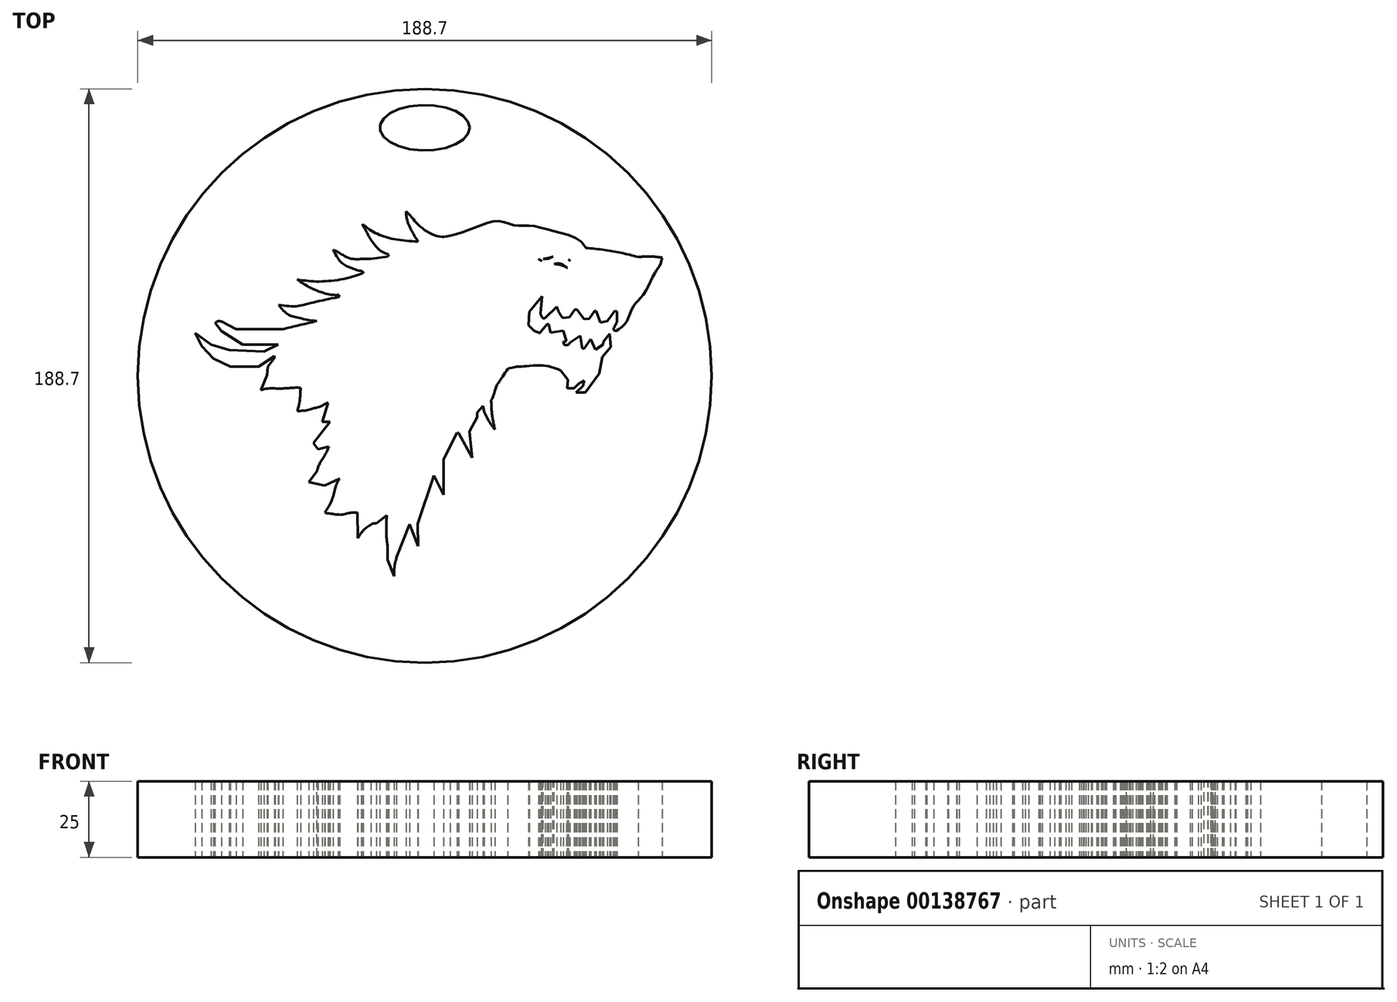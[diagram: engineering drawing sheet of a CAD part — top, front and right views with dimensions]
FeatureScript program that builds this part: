
annotation { "Feature Type Name" : "Feature", "Feature Type Description" : "" }
export const myFeature = defineFeature(function(context is Context, id is Id, definition is map)
    precondition{}
    {
        {
            var Q0;
            Q0=qCreatedBy(makeId("Top.planeOp"),FACE);
            var sketch = newSketch(context, id + "F0", { "sketchPlane" : qUnion([Q0])});
            skLineSegment(sketch, "E0", {"start": v(0, -46.34) * mm, "end": v(0, 97.64) * mm, "construction": true});
            skLineSegment(sketch, "E1", {"start": v(-98.9, 0) * mm, "end": v(160.67, 0) * mm, "construction": true});
            skFitSpline(sketch, "E2", {"points": [v(8.37, 46.02) * mm, v(16.5, 48.73) * mm, v(24.2, 50.9) * mm, v(29.67, 49.45) * mm, v(34.86, 49.36) * mm, v(43.4, 47.27) * mm, v(53, 42.06) * mm], "startDerivative": vector(47.53, 12.6) * mm, "endDerivative": vector(25.31, -53.78) * mm});
            skFitSpline(sketch, "E3", {"points": [v(53, 42.06) * mm, v(61.93, 40.92) * mm, v(70.2, 39.06) * mm], "startDerivative": vector(17.28, -1.4) * mm, "endDerivative": vector(17.12, -4.59) * mm});
            skFitSpline(sketch, "E4", {"points": [v(70.2, 39.06) * mm, v(73.91, 39.25) * mm, v(78, 38.88) * mm], "startDerivative": vector(7.53, 0.65) * mm, "endDerivative": vector(8.07, -1) * mm});
            skFitSpline(sketch, "E5", {"points": [v(78, 38.88) * mm, v(77.15, 36.05) * mm, v(75.57, 33.69) * mm, v(71.82, 26.58) * mm, v(68.71, 23.01) * mm, v(66.37, 17.92) * mm, v(62.79, 14.7) * mm], "startDerivative": vector(-2.44, -23.85) * mm, "endDerivative": vector(-25.04, -14.1) * mm});
            skLineSegment(sketch, "E6", {"start": v(62.79, 14.7) * mm, "end": v(62, 15.24) * mm});
            skLineSegment(sketch, "E7", {"start": v(62, 15.24) * mm, "end": v(63.2, 17.7) * mm});
            skLineSegment(sketch, "E8", {"start": v(63.2, 17.7) * mm, "end": v(63.2, 21.18) * mm});
            skLineSegment(sketch, "E9", {"start": v(63.2, 21.18) * mm, "end": v(62.45, 21.32) * mm});
            skLineSegment(sketch, "E10", {"start": v(62.45, 21.32) * mm, "end": v(60.09, 17.98) * mm});
            skLineSegment(sketch, "E11", {"start": v(60.09, 17.98) * mm, "end": v(57.72, 17.51) * mm});
            skLineSegment(sketch, "E12", {"start": v(57.72, 17.51) * mm, "end": v(56.32, 21.32) * mm});
            skLineSegment(sketch, "E13", {"start": v(56.32, 21.32) * mm, "end": v(55.78, 21.31) * mm});
            skLineSegment(sketch, "E14", {"start": v(55.78, 21.31) * mm, "end": v(54.02, 18.83) * mm});
            skLineSegment(sketch, "E15", {"start": v(54.02, 18.83) * mm, "end": v(52.38, 18.64) * mm});
            skLineSegment(sketch, "E16", {"start": v(52.38, 18.64) * mm, "end": v(49.96, 21.76) * mm});
            skLineSegment(sketch, "E17", {"start": v(49.96, 21.76) * mm, "end": v(49.36, 21.76) * mm});
            skLineSegment(sketch, "E18", {"start": v(49.36, 21.76) * mm, "end": v(47.55, 19.25) * mm});
            skLineSegment(sketch, "E19", {"start": v(47.55, 19.25) * mm, "end": v(45.5, 19.02) * mm});
            skFitSpline(sketch, "E20", {"points": [v(45.5, 19.02) * mm, v(44.43, 20.33) * mm, v(43.4, 22.76) * mm], "startDerivative": vector(-3.09, 1.68) * mm, "endDerivative": vector(-1.4, 5.58) * mm});
            skLineSegment(sketch, "E21", {"start": v(43.4, 22.76) * mm, "end": v(39.6, 19.05) * mm});
            skLineSegment(sketch, "E22", {"start": v(38.55, 26.15) * mm, "end": v(38.05, 20.53) * mm});
            skFitSpline(sketch, "E23", {"points": [v(38.05, 20.53) * mm, v(38.32, 19.7) * mm, v(38.9, 18.95) * mm, v(39.6, 19.05) * mm], "startDerivative": vector(0.59, -2.33) * mm, "endDerivative": vector(2.36, 0.9) * mm});
            skLineSegment(sketch, "E24", {"start": v(38.55, 26.15) * mm, "end": v(34.4, 21.11) * mm});
            skLineSegment(sketch, "E25", {"start": v(34.4, 21.11) * mm, "end": v(34.15, 16.58) * mm});
            skFitSpline(sketch, "E26", {"points": [v(34.15, 16.58) * mm, v(35.74, 14.98) * mm, v(37.83, 14.05) * mm], "startDerivative": vector(3.39, -3.5) * mm, "endDerivative": vector(3.98, -1.53) * mm});
            skLineSegment(sketch, "E27", {"start": v(37.83, 14.05) * mm, "end": v(40.2, 16.98) * mm});
            skLineSegment(sketch, "E28", {"start": v(40.2, 16.98) * mm, "end": v(40.7, 16.98) * mm});
            skLineSegment(sketch, "E29", {"start": v(40.7, 16.98) * mm, "end": v(41.3, 14.23) * mm});
            skLineSegment(sketch, "E30", {"start": v(41.3, 14.23) * mm, "end": v(45.53, 14.8) * mm});
            skLineSegment(sketch, "E31", {"start": v(45.53, 14.8) * mm, "end": v(46.61, 11.43) * mm});
            skLineSegment(sketch, "E32", {"start": v(46.61, 11.43) * mm, "end": v(45.6, 11.1) * mm});
            skLineSegment(sketch, "E33", {"start": v(47.71, 10.9) * mm, "end": v(51.18, 13.14) * mm});
            skFitSpline(sketch, "E34", {"points": [v(47.71, 10.9) * mm, v(47.14, 10.2) * mm, v(45.87, 10.24) * mm, v(45.6, 11.1) * mm], "startDerivative": vector(-1.25, -2.64) * mm, "endDerivative": vector(-0.16, 3.24) * mm});
            skLineSegment(sketch, "E35", {"start": v(51.18, 13.14) * mm, "end": v(51.76, 8.96) * mm});
            skLineSegment(sketch, "E36", {"start": v(51.76, 8.96) * mm, "end": v(52.35, 8.96) * mm});
            skLineSegment(sketch, "E37", {"start": v(52.35, 8.96) * mm, "end": v(54.64, 12.02) * mm});
            skLineSegment(sketch, "E38", {"start": v(54.64, 12.02) * mm, "end": v(56.15, 8.66) * mm});
            skLineSegment(sketch, "E39", {"start": v(56.15, 8.66) * mm, "end": v(58.7, 10.29) * mm});
            skLineSegment(sketch, "E40", {"start": v(58.7, 10.29) * mm, "end": v(58.8, 11.25) * mm});
            skLineSegment(sketch, "E41", {"start": v(58.8, 11.25) * mm, "end": v(60.75, 13.83) * mm});
            skLineSegment(sketch, "E42", {"start": v(60.75, 13.83) * mm, "end": v(61.12, 9.51) * mm});
            skLineSegment(sketch, "E43", {"start": v(61.12, 9.51) * mm, "end": v(58.37, 6.23) * mm});
            skLineSegment(sketch, "E44", {"start": v(58.37, 6.23) * mm, "end": v(57.38, 0.75) * mm});
            skLineSegment(sketch, "E45", {"start": v(57.38, 0.75) * mm, "end": v(52.78, -5.5) * mm});
            skLineSegment(sketch, "E46", {"start": v(52.78, -5.5) * mm, "end": v(49.73, -5.5) * mm});
            skLineSegment(sketch, "E47", {"start": v(49.73, -5.5) * mm, "end": v(52, -3.3) * mm});
            skLineSegment(sketch, "E48", {"start": v(52, -3.3) * mm, "end": v(52.42, -1.58) * mm});
            skLineSegment(sketch, "E49", {"start": v(52.42, -1.58) * mm, "end": v(50.65, -2.56) * mm});
            skLineSegment(sketch, "E50", {"start": v(50.65, -2.56) * mm, "end": v(49.07, -4.09) * mm});
            skLineSegment(sketch, "E51", {"start": v(49.07, -4.09) * mm, "end": v(46.86, -4.09) * mm});
            skLineSegment(sketch, "E52", {"start": v(46.86, -4.09) * mm, "end": v(47.02, -1.26) * mm});
            skLineSegment(sketch, "E53", {"start": v(47.02, -1.26) * mm, "end": v(44.6, 1.8) * mm});
            skFitSpline(sketch, "E54", {"points": [v(44.6, 1.8) * mm, v(38.62, 3.43) * mm, v(31.22, 2.96) * mm, v(30.22, 2.96) * mm, v(27.26, 2.3) * mm], "startDerivative": vector(-17, 7.19) * mm, "endDerivative": vector(-16.02, -4.1) * mm});
            skFitSpline(sketch, "E55", {"points": [v(27.26, 2.3) * mm, v(24.24, -2.27) * mm, v(23.71, -3.01) * mm, v(23.18, -4.49) * mm, v(21.86, -8.07) * mm], "startDerivative": vector(-9.48, -15.13) * mm, "endDerivative": vector(-7.44, -13.5) * mm});
            skFitSpline(sketch, "E56", {"points": [v(21.86, -8.07) * mm, v(22.1, -12.6) * mm, v(23.06, -17.73) * mm], "startDerivative": vector(0.3, -9.94) * mm, "endDerivative": vector(2.15, -9.73) * mm});
            skLineSegment(sketch, "E57", {"start": v(19.14, -9.9) * mm, "end": v(19.48, -11.87) * mm});
            skFitSpline(sketch, "E58", {"points": [v(19.48, -11.87) * mm, v(20.92, -14.56) * mm, v(23.06, -17.73) * mm], "startDerivative": vector(3.02, -5.51) * mm, "endDerivative": vector(4.86, -6.04) * mm});
            skLineSegment(sketch, "E59", {"start": v(19.14, -9.9) * mm, "end": v(17.18, -12.06) * mm});
            skLineSegment(sketch, "E60", {"start": v(17.18, -12.06) * mm, "end": v(17.18, -13.56) * mm});
            skLineSegment(sketch, "E61", {"start": v(17.18, -13.56) * mm, "end": v(14.64, -18.29) * mm});
            skLineSegment(sketch, "E62", {"start": v(14.64, -18.29) * mm, "end": v(15.58, -26.93) * mm});
            skLineSegment(sketch, "E63", {"start": v(15.58, -26.93) * mm, "end": v(11.12, -18.85) * mm});
            skLineSegment(sketch, "E64", {"start": v(11.12, -18.85) * mm, "end": v(10.6, -18.76) * mm});
            skLineSegment(sketch, "E65", {"start": v(10.6, -18.76) * mm, "end": v(6.22, -27.44) * mm});
            skLineSegment(sketch, "E66", {"start": v(6.22, -27.44) * mm, "end": v(6.17, -39.18) * mm});
            skLineSegment(sketch, "E67", {"start": v(6.17, -39.18) * mm, "end": v(3.07, -32.74) * mm});
            skLineSegment(sketch, "E68", {"start": v(3.07, -32.74) * mm, "end": v(-2.3, -48.66) * mm});
            skLineSegment(sketch, "E69", {"start": v(-2.3, -48.66) * mm, "end": v(-2.17, -56.06) * mm});
            skLineSegment(sketch, "E70", {"start": v(-2.17, -56.06) * mm, "end": v(-4.99, -48.79) * mm});
            skLineSegment(sketch, "E71", {"start": v(-4.99, -48.79) * mm, "end": v(-9.28, -59.71) * mm});
            skFitSpline(sketch, "E72", {"points": [v(-9.28, -59.71) * mm, v(-9.83, -61.89) * mm, v(-10.04, -63.68) * mm, v(-10.08, -65.99) * mm], "startDerivative": vector(-1.5, -7.23) * mm, "endDerivative": vector(0.61, -9.45) * mm});
            skLineSegment(sketch, "E73", {"start": v(-10.08, -65.99) * mm, "end": v(-12.22, -60.51) * mm});
            skLineSegment(sketch, "E74", {"start": v(-12.22, -60.51) * mm, "end": v(-12.22, -55.67) * mm});
            skFitSpline(sketch, "E75", {"points": [v(-12.22, -55.67) * mm, v(-12.62, -52.29) * mm, v(-12.62, -47.83) * mm, v(-12.44, -45.9) * mm], "startDerivative": vector(-2.35, 9.95) * mm, "endDerivative": vector(0.6, 6.7) * mm});
            skLineSegment(sketch, "E76", {"start": v(-12.44, -45.9) * mm, "end": v(-15.86, -48.6) * mm});
            skFitSpline(sketch, "E77", {"points": [v(-15.86, -48.6) * mm, v(-16.85, -48.6) * mm, v(-19.68, -50.34) * mm, v(-21.96, -53.33) * mm], "startDerivative": vector(-4.67, 0.75) * mm, "endDerivative": vector(-4.96, -8.28) * mm});
            skLineSegment(sketch, "E78", {"start": v(-21.96, -53.33) * mm, "end": v(-22.2, -45.03) * mm});
            skFitSpline(sketch, "E79", {"points": [v(-22.2, -45.03) * mm, v(-23.7, -45.03) * mm, v(-25.38, -45.24) * mm, v(-27.7, -45.69) * mm, v(-30.45, -45.39) * mm, v(-32.84, -45.03) * mm], "startDerivative": vector(-10.12, -0.25) * mm, "endDerivative": vector(-8.12, 2.64) * mm});
            skFitSpline(sketch, "E80", {"points": [v(-32.84, -45.03) * mm, v(-30.46, -40.57) * mm, v(-29.33, -36.68) * mm, v(-27.93, -33.79) * mm], "startDerivative": vector(7.96, 12) * mm, "endDerivative": vector(7.34, 9.15) * mm});
            skLineSegment(sketch, "E81", {"start": v(-27.93, -33.79) * mm, "end": v(-33, -36.1) * mm});
            skLineSegment(sketch, "E82", {"start": v(-33, -36.1) * mm, "end": v(-38.14, -34.9) * mm});
            skLineSegment(sketch, "E83", {"start": v(-38.14, -34.9) * mm, "end": v(-35.38, -31.25) * mm});
            skFitSpline(sketch, "E84", {"points": [v(-35.38, -31.25) * mm, v(-34.63, -29.02) * mm, v(-32.62, -25.74) * mm, v(-31.58, -23.28) * mm], "startDerivative": vector(1.7, 7.16) * mm, "endDerivative": vector(2.6, 7.43) * mm});
            skLineSegment(sketch, "E85", {"start": v(-31.58, -23.28) * mm, "end": v(-35.08, -24.1) * mm});
            skLineSegment(sketch, "E86", {"start": v(-35.08, -24.1) * mm, "end": v(-36.57, -22.16) * mm});
            skLineSegment(sketch, "E87", {"start": v(-36.57, -22.16) * mm, "end": v(-31.2, -15.15) * mm});
            skLineSegment(sketch, "E88", {"start": v(-31.2, -15.15) * mm, "end": v(-33.74, -15.15) * mm});
            skLineSegment(sketch, "E89", {"start": v(-33.74, -15.15) * mm, "end": v(-31.79, -8.9) * mm});
            skFitSpline(sketch, "E90", {"points": [v(-31.79, -8.9) * mm, v(-33.97, -9.91) * mm, v(-36.14, -10.62) * mm, v(-38.4, -11.28) * mm, v(-41.9, -11.6) * mm], "startDerivative": vector(-6.1, 1.36) * mm, "endDerivative": vector(-8.76, -0.8) * mm});
            skFitSpline(sketch, "E91", {"points": [v(-41.9, -11.6) * mm, v(-41.13, -8.29) * mm, v(-40.83, -3.95) * mm], "startDerivative": vector(1.85, 6.75) * mm, "endDerivative": vector(0.43, 8.1) * mm});
            skFitSpline(sketch, "E92", {"points": [v(-40.83, -3.95) * mm, v(-45.11, -4.06) * mm, v(-48.54, -4.17) * mm, v(-53.9, -4.78) * mm], "startDerivative": vector(-10.76, 1.27) * mm, "endDerivative": vector(-11.93, -6.43) * mm});
            skLineSegment(sketch, "E93", {"start": v(-53.9, -4.78) * mm, "end": v(-51.88, 0.27) * mm});
            skLineSegment(sketch, "E94", {"start": v(-51.88, 0.27) * mm, "end": v(-51.63, 3.08) * mm});
            skLineSegment(sketch, "E95", {"start": v(-51.63, 3.08) * mm, "end": v(-49.22, 6.21) * mm});
            skLineSegment(sketch, "E96", {"start": v(-49.22, 6.21) * mm, "end": v(-49.5, 6.43) * mm});
            skLineSegment(sketch, "E97", {"start": v(-49.5, 6.43) * mm, "end": v(-54.64, 2.98) * mm});
            skLineSegment(sketch, "E98", {"start": v(-54.64, 2.98) * mm, "end": v(-63.96, 2.98) * mm});
            skLineSegment(sketch, "E99", {"start": v(-63.96, 2.98) * mm, "end": v(-69.48, 5.65) * mm});
            skLineSegment(sketch, "E100", {"start": v(-69.48, 5.65) * mm, "end": v(-73.26, 9.73) * mm});
            skLineSegment(sketch, "E101", {"start": v(-73.26, 9.73) * mm, "end": v(-75.45, 14.1) * mm});
            skLineSegment(sketch, "E102", {"start": v(-75.45, 14.1) * mm, "end": v(-70.28, 10.27) * mm});
            skLineSegment(sketch, "E103", {"start": v(-70.28, 10.27) * mm, "end": v(-64.26, 8.53) * mm});
            skLineSegment(sketch, "E104", {"start": v(-64.26, 8.53) * mm, "end": v(-52.92, 7.99) * mm});
            skLineSegment(sketch, "E105", {"start": v(-52.92, 7.99) * mm, "end": v(-48.15, 10.22) * mm});
            skLineSegment(sketch, "E106", {"start": v(-48.15, 10.22) * mm, "end": v(-59.86, 10.22) * mm});
            skLineSegment(sketch, "E107", {"start": v(-59.86, 10.22) * mm, "end": v(-66.87, 14.75) * mm});
            skLineSegment(sketch, "E108", {"start": v(-66.87, 14.75) * mm, "end": v(-68.94, 17.44) * mm});
            skLineSegment(sketch, "E109", {"start": v(-66.8, 17.83) * mm, "end": v(-62.02, 15.35) * mm});
            skLineSegment(sketch, "E110", {"start": v(-62.02, 15.35) * mm, "end": v(-46.65, 15.35) * mm});
            skFitSpline(sketch, "E111", {"points": [v(-46.65, 15.35) * mm, v(-41.43, 16.6) * mm, v(-35.5, 17.98) * mm], "startDerivative": vector(10.61, 2.53) * mm, "endDerivative": vector(11.66, 2.74) * mm});
            skFitSpline(sketch, "E112", {"points": [v(-35.5, 17.98) * mm, v(-41.82, 19.11) * mm, v(-44.94, 20.17) * mm, v(-48, 23.3) * mm], "startDerivative": vector(-16.98, 1.76) * mm, "endDerivative": vector(-6.9, 10.96) * mm});
            skFitSpline(sketch, "E113", {"points": [v(-48, 23.3) * mm, v(-42.22, 22.9) * mm, v(-37.6, 23.9) * mm, v(-28.48, 25.89) * mm], "startDerivative": vector(19.28, -2.54) * mm, "endDerivative": vector(24.98, 5.08) * mm});
            skFitSpline(sketch, "E114", {"points": [v(-28.48, 26.58) * mm, v(-31.56, 26.78) * mm, v(-37.4, 28.87) * mm, v(-41.92, 31.66) * mm], "startDerivative": vector(-10.5, -0.18) * mm, "endDerivative": vector(-11.9, 8.2) * mm});
            skArc(sketch, "E115", {"start": v(-28.48, 25.89) * mm, "mid": v(-28.12, 26.23) * mm, "end": v(-28.48, 26.58) * mm});
            skFitSpline(sketch, "E116", {"points": [v(-68.94, 17.44) * mm, v(-67.92, 17.97) * mm, v(-66.8, 17.83) * mm], "startDerivative": vector(1.97, 1.4) * mm, "endDerivative": vector(2.31, -0.6) * mm});
            skFitSpline(sketch, "E117", {"points": [v(-41.92, 31.66) * mm, v(-36.84, 31.05) * mm, v(-31.36, 31.2) * mm, v(-24.7, 32.3) * mm, v(-20.72, 33.69) * mm], "startDerivative": vector(20.83, -3.13) * mm, "endDerivative": vector(16.42, 6.68) * mm});
            skFitSpline(sketch, "E118", {"points": [v(-20.72, 33.69) * mm, v(-20.23, 34.03) * mm, v(-20.92, 34.48) * mm], "startDerivative": vector(2.1, 0.45) * mm, "endDerivative": vector(-2.36, 1.12) * mm});
            skFitSpline(sketch, "E119", {"points": [v(-20.92, 34.48) * mm, v(-24.7, 35.66) * mm, v(-27.36, 37.18) * mm, v(-30.15, 41.53) * mm], "startDerivative": vector(-10.4, 0.84) * mm, "endDerivative": vector(-5.33, 11.62) * mm});
            skFitSpline(sketch, "E120", {"points": [v(-30.15, 41.53) * mm, v(-27.9, 40.27) * mm, v(-24.38, 38.58) * mm, v(-20.96, 38.41) * mm, v(-17.67, 38.48) * mm], "startDerivative": vector(9.55, -5.2) * mm, "endDerivative": vector(13.09, 0.11) * mm});
            skLineSegment(sketch, "E121", {"start": v(-17.67, 38.48) * mm, "end": v(-12.16, 39.28) * mm});
            skLineSegment(sketch, "E122", {"start": v(-12.16, 39.28) * mm, "end": v(-11.8, 39.9) * mm});
            skFitSpline(sketch, "E123", {"points": [v(-11.8, 39.9) * mm, v(-14.65, 41.23) * mm, v(-17.8, 44.9) * mm, v(-18.97, 46.96) * mm, v(-20.52, 49.83) * mm], "startDerivative": vector(-11.73, 3.62) * mm, "endDerivative": vector(-6.78, 12.4) * mm});
            skFitSpline(sketch, "E124", {"points": [v(-20.52, 49.83) * mm, v(-16.53, 47.15) * mm, v(-10.66, 45.04) * mm, v(-2.16, 44.15) * mm], "startDerivative": vector(13.1, -9.77) * mm, "endDerivative": vector(23.04, -1.36) * mm});
            skFitSpline(sketch, "E125", {"points": [v(-2.16, 44.15) * mm, v(-3.8, 46.7) * mm, v(-5.85, 51.28) * mm, v(-6.14, 54.04) * mm], "startDerivative": vector(-5.04, 7.36) * mm, "endDerivative": vector(-0.06, 8.63) * mm});
            skFitSpline(sketch, "E126", {"points": [v(-6.14, 54.04) * mm, v(-4.54, 52.44) * mm, v(-1.41, 49.01) * mm, v(4.44, 45.88) * mm, v(8.37, 46.02) * mm], "startDerivative": vector(8.45, -7.78) * mm, "endDerivative": vector(15.33, 2.76) * mm});
            skFitSpline(sketch, "E127", {"points": [v(37.42, 38.31) * mm, v(40.78, 37) * mm, v(44.4, 36.52) * mm, v(47.82, 34.96) * mm], "startDerivative": vector(9.91, -4.83) * mm, "endDerivative": vector(9.8, -5.8) * mm});
            skFitSpline(sketch, "E128", {"points": [v(37.42, 38.31) * mm, v(40.89, 38.8) * mm, v(43.76, 39.66) * mm, v(46.07, 39.28) * mm, v(47.7, 37.83) * mm], "startDerivative": vector(15.86, 1.57) * mm, "endDerivative": vector(4.95, -5.03) * mm});
            skLineSegment(sketch, "E129", {"start": v(47.7, 37.83) * mm, "end": v(47.82, 34.96) * mm});
            skSolve(sketch);
        }
        {
            var Q0;
            Q0=makeQuery(id+"F0.imprint","IMPRINT",FACE,{"disambiguationData":[TD([[makeQuery(id+"F0.imprint","IMPRINT",EDGE,{"derivedFrom":sQuery(id+"F0.wireOp",EDGE,"E2")}),-1.0]])]});
            extrude(context, id + "F1", {"entities" : qUnion([Q0]), "depth" : 25 * mm});
        }
        {
            var Q0;
            Q0=qCreatedBy(makeId("Top.planeOp"),FACE);
            var sketch = newSketch(context, id + "F2", { "sketchPlane" : qUnion([Q0])});
            skCircle(sketch, "E130", {"center": v(0, 0) * mm, "radius": 94.35 * mm});
            skEllipse(sketch, "E131", {"center": v(0, 81.58) * mm, "majorRadius": 14.76 * mm, "minorRadius": 7.47 * mm, "majorAxis": v(1, 0)});
            skSolve(sketch);
        }
        {
            var Q0;
            Q0=makeQuery(id+"F2.imprint","IMPRINT",FACE,{"disambiguationData":[TD([[makeQuery(id+"F2.imprint","IMPRINT",EDGE,{"derivedFrom":sQuery(id+"F2.wireOp",EDGE,"E130")}),1.0]])]});
            extrude(context, id + "F3", {"entities" : qUnion([Q0]), "depth" : 25 * mm});
        }
        {
            var Q0;
            Q0=makeQuery(id+"F1.opExtrude","SWEPT_BODY",BODY,{"disambiguationData":[OSD([sQuery(id+"F0.wireOp",EDGE,"E2"),sQuery(id+"F0.wireOp",EDGE,"E3"),sQuery(id+"F0.wireOp",EDGE,"E4"),sQuery(id+"F0.wireOp",EDGE,"E5"),sQuery(id+"F0.wireOp",EDGE,"E6"),sQuery(id+"F0.wireOp",EDGE,"E7"),sQuery(id+"F0.wireOp",EDGE,"E8"),sQuery(id+"F0.wireOp",EDGE,"E9"),sQuery(id+"F0.wireOp",EDGE,"E10"),sQuery(id+"F0.wireOp",EDGE,"E11"),sQuery(id+"F0.wireOp",EDGE,"E12"),sQuery(id+"F0.wireOp",EDGE,"E13"),sQuery(id+"F0.wireOp",EDGE,"E14"),sQuery(id+"F0.wireOp",EDGE,"E15"),sQuery(id+"F0.wireOp",EDGE,"E16"),sQuery(id+"F0.wireOp",EDGE,"E17"),sQuery(id+"F0.wireOp",EDGE,"E18"),sQuery(id+"F0.wireOp",EDGE,"E19"),sQuery(id+"F0.wireOp",EDGE,"E20"),sQuery(id+"F0.wireOp",EDGE,"E21"),sQuery(id+"F0.wireOp",EDGE,"E22"),sQuery(id+"F0.wireOp",EDGE,"E23"),sQuery(id+"F0.wireOp",EDGE,"E24"),sQuery(id+"F0.wireOp",EDGE,"E25"),sQuery(id+"F0.wireOp",EDGE,"E26"),sQuery(id+"F0.wireOp",EDGE,"E27"),sQuery(id+"F0.wireOp",EDGE,"E28"),sQuery(id+"F0.wireOp",EDGE,"E29"),sQuery(id+"F0.wireOp",EDGE,"E30"),sQuery(id+"F0.wireOp",EDGE,"E31"),sQuery(id+"F0.wireOp",EDGE,"E32"),sQuery(id+"F0.wireOp",EDGE,"E33"),sQuery(id+"F0.wireOp",EDGE,"E34"),sQuery(id+"F0.wireOp",EDGE,"E35"),sQuery(id+"F0.wireOp",EDGE,"E36"),sQuery(id+"F0.wireOp",EDGE,"E37"),sQuery(id+"F0.wireOp",EDGE,"E38"),sQuery(id+"F0.wireOp",EDGE,"E39"),sQuery(id+"F0.wireOp",EDGE,"E40"),sQuery(id+"F0.wireOp",EDGE,"E41"),sQuery(id+"F0.wireOp",EDGE,"E42"),sQuery(id+"F0.wireOp",EDGE,"E43"),sQuery(id+"F0.wireOp",EDGE,"E44"),sQuery(id+"F0.wireOp",EDGE,"E45"),sQuery(id+"F0.wireOp",EDGE,"E46"),sQuery(id+"F0.wireOp",EDGE,"E47"),sQuery(id+"F0.wireOp",EDGE,"E48"),sQuery(id+"F0.wireOp",EDGE,"E49"),sQuery(id+"F0.wireOp",EDGE,"E50"),sQuery(id+"F0.wireOp",EDGE,"E51"),sQuery(id+"F0.wireOp",EDGE,"E52"),sQuery(id+"F0.wireOp",EDGE,"E53"),sQuery(id+"F0.wireOp",EDGE,"E54"),sQuery(id+"F0.wireOp",EDGE,"E55"),sQuery(id+"F0.wireOp",EDGE,"E56"),sQuery(id+"F0.wireOp",EDGE,"E57"),sQuery(id+"F0.wireOp",EDGE,"E58"),sQuery(id+"F0.wireOp",EDGE,"E59"),sQuery(id+"F0.wireOp",EDGE,"E60"),sQuery(id+"F0.wireOp",EDGE,"E61"),sQuery(id+"F0.wireOp",EDGE,"E62"),sQuery(id+"F0.wireOp",EDGE,"E63"),sQuery(id+"F0.wireOp",EDGE,"E64"),sQuery(id+"F0.wireOp",EDGE,"E65"),sQuery(id+"F0.wireOp",EDGE,"E66"),sQuery(id+"F0.wireOp",EDGE,"E67"),sQuery(id+"F0.wireOp",EDGE,"E68"),sQuery(id+"F0.wireOp",EDGE,"E69"),sQuery(id+"F0.wireOp",EDGE,"E70"),sQuery(id+"F0.wireOp",EDGE,"E71"),sQuery(id+"F0.wireOp",EDGE,"E72"),sQuery(id+"F0.wireOp",EDGE,"E73"),sQuery(id+"F0.wireOp",EDGE,"E74"),sQuery(id+"F0.wireOp",EDGE,"E75"),sQuery(id+"F0.wireOp",EDGE,"E76"),sQuery(id+"F0.wireOp",EDGE,"E77"),sQuery(id+"F0.wireOp",EDGE,"E78"),sQuery(id+"F0.wireOp",EDGE,"E79"),sQuery(id+"F0.wireOp",EDGE,"E80"),sQuery(id+"F0.wireOp",EDGE,"E81"),sQuery(id+"F0.wireOp",EDGE,"E82"),sQuery(id+"F0.wireOp",EDGE,"E83"),sQuery(id+"F0.wireOp",EDGE,"E84"),sQuery(id+"F0.wireOp",EDGE,"E85"),sQuery(id+"F0.wireOp",EDGE,"E86"),sQuery(id+"F0.wireOp",EDGE,"E87"),sQuery(id+"F0.wireOp",EDGE,"E88"),sQuery(id+"F0.wireOp",EDGE,"E89"),sQuery(id+"F0.wireOp",EDGE,"E90"),sQuery(id+"F0.wireOp",EDGE,"E91"),sQuery(id+"F0.wireOp",EDGE,"E92"),sQuery(id+"F0.wireOp",EDGE,"E93"),sQuery(id+"F0.wireOp",EDGE,"E94"),sQuery(id+"F0.wireOp",EDGE,"E95"),sQuery(id+"F0.wireOp",EDGE,"E96"),sQuery(id+"F0.wireOp",EDGE,"E97"),sQuery(id+"F0.wireOp",EDGE,"E98"),sQuery(id+"F0.wireOp",EDGE,"E99"),sQuery(id+"F0.wireOp",EDGE,"E100"),sQuery(id+"F0.wireOp",EDGE,"E101"),sQuery(id+"F0.wireOp",EDGE,"E102"),sQuery(id+"F0.wireOp",EDGE,"E103"),sQuery(id+"F0.wireOp",EDGE,"E104"),sQuery(id+"F0.wireOp",EDGE,"E105"),sQuery(id+"F0.wireOp",EDGE,"E106"),sQuery(id+"F0.wireOp",EDGE,"E107"),sQuery(id+"F0.wireOp",EDGE,"E108"),sQuery(id+"F0.wireOp",EDGE,"E109"),sQuery(id+"F0.wireOp",EDGE,"E110"),sQuery(id+"F0.wireOp",EDGE,"E111"),sQuery(id+"F0.wireOp",EDGE,"E112"),sQuery(id+"F0.wireOp",EDGE,"E113"),sQuery(id+"F0.wireOp",EDGE,"E114"),sQuery(id+"F0.wireOp",EDGE,"E115"),sQuery(id+"F0.wireOp",EDGE,"E116"),sQuery(id+"F0.wireOp",EDGE,"E117"),sQuery(id+"F0.wireOp",EDGE,"E118"),sQuery(id+"F0.wireOp",EDGE,"E119"),sQuery(id+"F0.wireOp",EDGE,"E120"),sQuery(id+"F0.wireOp",EDGE,"E121"),sQuery(id+"F0.wireOp",EDGE,"E122"),sQuery(id+"F0.wireOp",EDGE,"E123"),sQuery(id+"F0.wireOp",EDGE,"E124"),sQuery(id+"F0.wireOp",EDGE,"E125"),sQuery(id+"F0.wireOp",EDGE,"E126"),sQuery(id+"F0.wireOp",EDGE,"E127"),sQuery(id+"F0.wireOp",EDGE,"E128"),sQuery(id+"F0.wireOp",EDGE,"E129")])]});
            var Q1;
            Q1=makeQuery(id+"F3.opExtrude","SWEPT_BODY",BODY,{"disambiguationData":[OSD([sQuery(id+"F2.wireOp",EDGE,"E130"),sQuery(id+"F2.wireOp",EDGE,"E131")])]});
            booleanBodies(context, id + "F4", {"operationType" : BooleanOperationType.SUBTRACTION, "tools" : qUnion([Q0]), "targets" : qUnion([Q1])});
        }
        {
            var Q0;
            {var subQ0=sQuery(id+"F2.wireOp",EDGE,"E130");var subQ1=sQuery(id+"F2.wireOp",EDGE,"E131");Q0=makeQuery(id+"F4.opBoolean","SPLIT",FACE,{"disambiguationData":[TD([makeQuery(id+"F1.opExtrude","SWEPT_FACE",FACE,{"disambiguationData":[OSD([sQuery(id+"F0.wireOp",EDGE,"E2")])]})])],"derivedFrom":makeQuery(id+"F3.opExtrude","CAP_FACE",FACE,{"disambiguationData":[OSD([subQ0,subQ1])],"isStart":false})});}
            var sketch = newSketch(context, id + "F5", { "sketchPlane" : qUnion([Q0])});
            skFitSpline(sketch, "E132.0.0", {"points": [v(37.42, 38.31) * mm, v(38.51, 37.78) * mm, v(40.7, 36.72) * mm, v(44.49, 36.85) * mm, v(46.72, 35.61) * mm, v(47.82, 34.96) * mm]});
            skLineSegment(sketch, "E132.0.1", {"start": v(47.82, 34.96) * mm, "end": v(47.7, 37.83) * mm});
            skFitSpline(sketch, "E132.0.2", {"points": [v(47.7, 37.83) * mm, v(47.34, 38.2) * mm, v(46.13, 39.6) * mm, v(43.7, 39.9) * mm, v(40.76, 38.57) * mm, v(38.92, 38.46) * mm, v(37.42, 38.31) * mm]});
            skSolve(sketch);
        }
        {
            var Q0;
            Q0=makeQuery(id+"F5.imprint","IMPRINT",FACE,{"disambiguationData":[TD([[makeQuery(id+"F5.imprint","IMPRINT",EDGE,{"derivedFrom":sQuery(id+"F5.wireOp",EDGE,"E132.0.0")}),1.0]])]});
            extrude(context, id + "F6", {"entities" : qUnion([Q0]), "operationType" : NewBodyOperationType.REMOVE, "oppositeDirection" : true, "depth" : 25 * mm});
        }
    });
